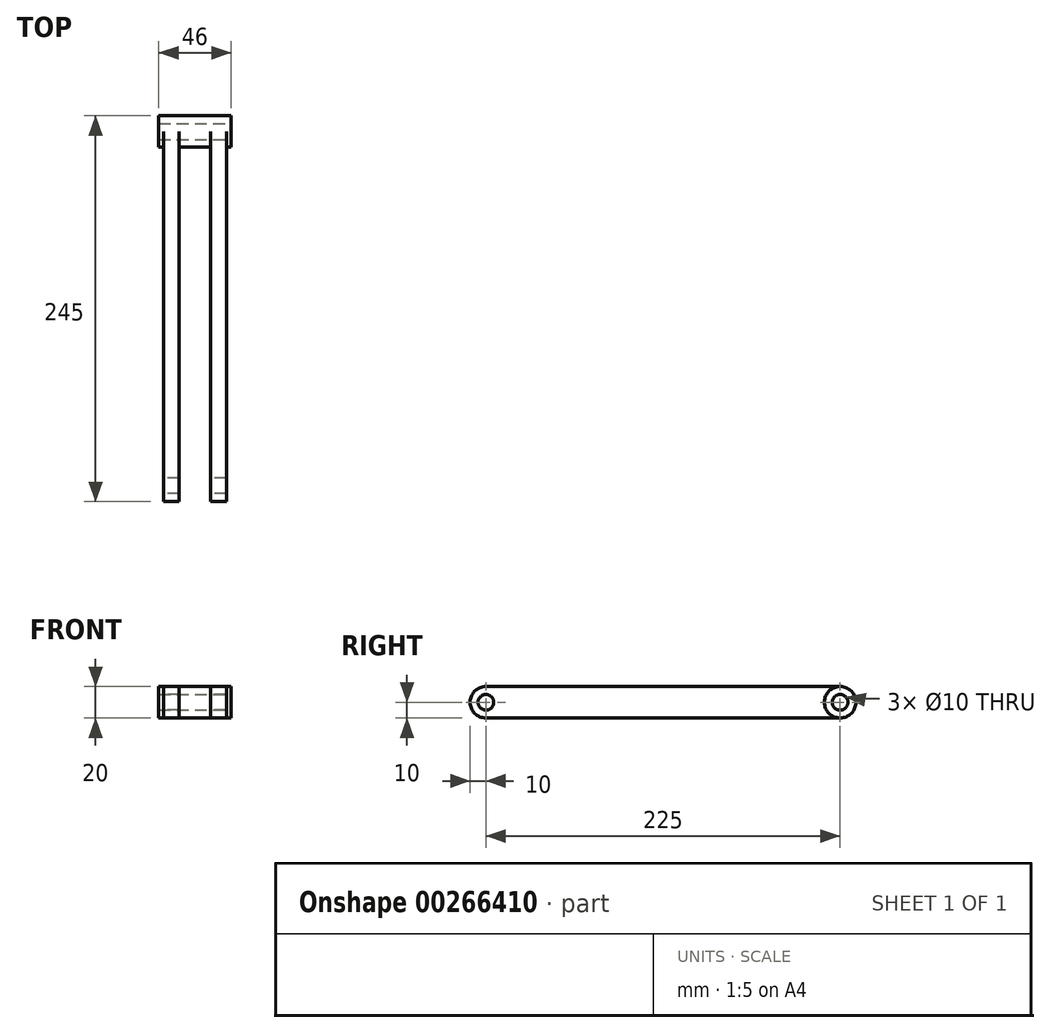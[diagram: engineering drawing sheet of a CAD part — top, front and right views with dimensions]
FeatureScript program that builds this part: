
annotation { "Feature Type Name" : "Feature", "Feature Type Description" : "" }
export const myFeature = defineFeature(function(context is Context, id is Id, definition is map)
    precondition{}
    {
        {
            var Q0;
            Q0=qCreatedBy(makeId("Right.planeOp"),FACE);
            var sketch = newSketch(context, id + "F0", { "sketchPlane" : qUnion([Q0])});
            skCircle(sketch, "E0", {"center": v(0, 0) * mm, "radius": 10 * mm});
            skCircle(sketch, "E1", {"center": v(0, 0) * mm, "radius": 5 * mm});
            skLineSegment(sketch, "E2", {"start": v(0, 0) * mm, "end": v(10, 0) * mm, "construction": true});
            skLineSegment(sketch, "E3", {"start": v(10, 0) * mm, "end": v(-235, 0) * mm, "construction": true});
            skLineSegment(sketch, "E4", {"start": v(0, 0) * mm, "end": v(0, 10) * mm, "construction": true});
            skLineSegment(sketch, "E5", {"start": v(-235, 0) * mm, "end": v(-225, 0) * mm, "construction": true});
            skCircle(sketch, "E6", {"center": v(-225, 0) * mm, "radius": 10 * mm});
            skLineSegment(sketch, "E7", {"start": v(0, 10) * mm, "end": v(-225, 10) * mm});
            skLineSegment(sketch, "E8", {"start": v(-225, 0) * mm, "end": v(-225, -10) * mm, "construction": true});
            skLineSegment(sketch, "E9", {"start": v(-225, -10) * mm, "end": v(0, -10) * mm});
            skCircle(sketch, "E10", {"center": v(-225, 0) * mm, "radius": 5 * mm});
            skSolve(sketch);
        }
        {
            var Q0;
            Q0=makeQuery(id+"F0.imprint","IMPRINT",FACE,{"disambiguationData":[TD([[makeQuery(id+"F0.imprint","IMPRINT",EDGE,{"derivedFrom":sQuery(id+"F0.wireOp",EDGE,"E0")}),1.0]])]});
            extrude(context, id + "F1", {"entities" : qUnion([Q0]), "oppositeDirection" : true, "depth" : 30 * mm, "hasSecondDirection" : true, "secondDirectionOppositeDirection" : false, "secondDirectionDepth" : 10 * mm});
        }
        {
            var Q0;
            {var subQ0=sQuery(id+"F0.wireOp",EDGE,"E7");Q0=makeQuery(id+"F0.imprint","IMPRINT",FACE,{"disambiguationData":[TD([[makeQuery(id+"F0.imprint","IMPRINT",EDGE,{"derivedFrom":subQ0}),1.0]])]});}
            var Q1;
            Q1=makeQuery(id+"F0.imprint","IMPRINT",FACE,{"disambiguationData":[TD([[makeQuery(id+"F0.imprint","IMPRINT",EDGE,{"derivedFrom":sQuery(id+"F0.wireOp",EDGE,"E10")}),-1.0]])]});
            extrude(context, id + "F2", {"entities" : qUnion([Q0, Q1]), "operationType" : NewBodyOperationType.ADD, "depth" : 10 * mm});
        }
        {
            var Q0;
            {var subQ0=sQuery(id+"F0.wireOp",EDGE,"E0");Q0=makeQuery(id+"F2.boolean.opBoolean","MERGE",FACE,{"derivedFrom":[makeQuery(id+"F1.opExtrude","CAP_FACE",FACE,{"disambiguationData":[OSD([subQ0,sQuery(id+"F0.wireOp",EDGE,"E1")])],"isStart":true}),makeQuery(id+"F2.opExtrude","CAP_FACE",FACE,{"disambiguationData":[OSD([subQ0,sQuery(id+"F0.wireOp",EDGE,"E6"),sQuery(id+"F0.wireOp",EDGE,"E7"),sQuery(id+"F0.wireOp",EDGE,"E9"),sQuery(id+"F0.wireOp",EDGE,"E10")])],"isStart":false})]});}
            var sketch = newSketch(context, id + "F3", { "sketchPlane" : qUnion([Q0])});
            skCircle(sketch, "E11", {"center": v(0, 0) * mm, "radius": 5 * mm});
            skCircle(sketch, "E12", {"center": v(0, 0) * mm, "radius": 10 * mm});
            skSolve(sketch);
        }
        {
            var Q0;
            Q0=makeQuery(id+"F3.imprint","IMPRINT",FACE,{"disambiguationData":[TD([[makeQuery(id+"F3.imprint","IMPRINT",EDGE,{"derivedFrom":sQuery(id+"F3.wireOp",EDGE,"E11")}),-1.0]])]});
            extrude(context, id + "F4", {"entities" : qUnion([Q0]), "operationType" : NewBodyOperationType.ADD, "depth" : 3 * mm});
        }
        {
            var Q0;
            Q0=makeQuery(id+"F1.opExtrude","CAP_FACE",FACE,{"disambiguationData":[OSD([sQuery(id+"F0.wireOp",EDGE,"E0"),sQuery(id+"F0.wireOp",EDGE,"E1")])],"isStart":false});
            var sketch = newSketch(context, id + "F5", { "sketchPlane" : qUnion([Q0])});
            skCircle(sketch, "E13", {"center": v(0, 0) * mm, "radius": 10 * mm});
            skCircle(sketch, "E14", {"center": v(0, 0) * mm, "radius": 5 * mm});
            skLineSegment(sketch, "E15", {"start": v(0, 0) * mm, "end": v(225, 0) * mm, "construction": true});
            skCircle(sketch, "E16", {"center": v(225, 0) * mm, "radius": 5 * mm});
            skCircle(sketch, "E17", {"center": v(225, 0) * mm, "radius": 10 * mm});
            skLineSegment(sketch, "E18", {"start": v(0, 0) * mm, "end": v(0, 10) * mm, "construction": true});
            skLineSegment(sketch, "E19", {"start": v(225, 0) * mm, "end": v(225, -10) * mm, "construction": true});
            skLineSegment(sketch, "E20", {"start": v(225, -10) * mm, "end": v(0, -10) * mm});
            skLineSegment(sketch, "E21", {"start": v(0, 10) * mm, "end": v(225, 10) * mm});
            skSolve(sketch);
        }
        {
            var Q0;
            {var subQ0=sQuery(id+"F5.wireOp",EDGE,"E20");Q0=makeQuery(id+"F5.imprint","IMPRINT",FACE,{"disambiguationData":[TD([[makeQuery(id+"F5.imprint","IMPRINT",EDGE,{"derivedFrom":subQ0}),-1.0]])]});}
            var Q1;
            Q1=makeQuery(id+"F5.imprint","IMPRINT",FACE,{"disambiguationData":[TD([[makeQuery(id+"F5.imprint","IMPRINT",EDGE,{"derivedFrom":sQuery(id+"F5.wireOp",EDGE,"E16")}),-1.0]])]});
            extrude(context, id + "F6", {"entities" : qUnion([Q0, Q1]), "operationType" : NewBodyOperationType.ADD, "oppositeDirection" : true, "depth" : 10 * mm});
        }
        {
            var Q0;
            Q0=makeQuery(id+"F6.boolean.opBoolean","MERGE",FACE,{"derivedFrom":[makeQuery(id+"F1.opExtrude","CAP_FACE",FACE,{"disambiguationData":[OSD([sQuery(id+"F0.wireOp",EDGE,"E0"),sQuery(id+"F0.wireOp",EDGE,"E1")])],"isStart":false}),makeQuery(id+"F6.opExtrude","CAP_FACE",FACE,{"disambiguationData":[OSD([sQuery(id+"F5.wireOp",EDGE,"E13"),sQuery(id+"F5.wireOp",EDGE,"E16"),sQuery(id+"F5.wireOp",EDGE,"E17"),sQuery(id+"F5.wireOp",EDGE,"E20"),sQuery(id+"F5.wireOp",EDGE,"E21")])],"isStart":true})]});
            var sketch = newSketch(context, id + "F7", { "sketchPlane" : qUnion([Q0])});
            skCircle(sketch, "E22", {"center": v(0, 0) * mm, "radius": 5 * mm});
            skCircle(sketch, "E23", {"center": v(0, 0) * mm, "radius": 10 * mm});
            skSolve(sketch);
        }
        {
            var Q0;
            Q0=makeQuery(id+"F7.imprint","IMPRINT",FACE,{"disambiguationData":[TD([[makeQuery(id+"F7.imprint","IMPRINT",EDGE,{"derivedFrom":sQuery(id+"F7.wireOp",EDGE,"E22")}),1.0]])]});
            var Q1;
            Q1=sQuery(id+"F7.wireOp",EDGE,"E23");
            extrude(context, id + "F8", {"entities" : qUnion([Q0]), "operationType" : NewBodyOperationType.ADD, "surfaceEntities" : qUnion([Q1]), "depth" : 3 * mm});
        }
    });
